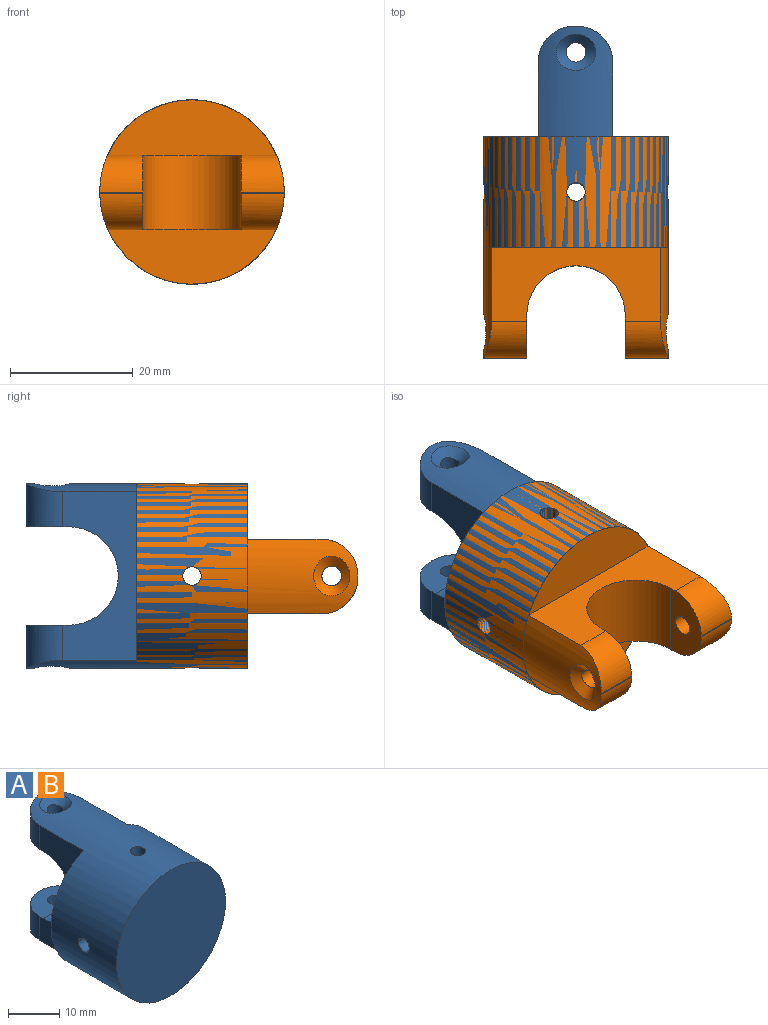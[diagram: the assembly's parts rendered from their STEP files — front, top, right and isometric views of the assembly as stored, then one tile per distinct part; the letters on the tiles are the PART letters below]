
ASSEMBLY  parts=2 mates=1
PART A: 23 faces, bbox 30x36x30 mm
  f0: cylinder r=1.5mm len=14.93mm, axis (1,0,0), area 132.6mm2, adj f2,f21,f22
  f1: plane 7x0.16mm, normal (0,1,0), area 1.1mm2, adj f2,f6,f14,f15
  f2: cylinder r=15mm len=36mm, axis (0,1,0), area 2026.3mm2, adj f0,f1,f3,f7,f10,f11,f12,f13
  f3: plane 7x0.16mm, normal (0,1,0), area 1.1mm2, adj f2,f5,f16,f17
  f4: cylinder r=8mm len=16mm, axis (1,0,0), area 305.7mm2, adj f5,f6,f11,f13
  f5: plane 12.16x7mm, normal (0,0,1), area 61.7mm2, adj f3,f4,f9,f11,f13,f16,f17
  f6: plane 12.16x7mm, normal (0,0,-1), area 61.7mm2, adj f1,f4,f8,f11,f13,f14,f15
  f7: plane 30x30mm, normal (0,-1,0), area 706.9mm2, adj f2
  f8: cylinder r=1.6mm len=5.65mm, axis (0,0,1), area 56.8mm2, adj f6,f18
  f9: cylinder r=1.6mm len=5.33mm, axis (0,0,1), area 53.6mm2, adj f5,f19
  f10: plane 27.5x9mm, normal (0,1,0), area 178.4mm2, adj f2,f11
  f11: plane 27.5x12mm, normal (1,0,0), area 213.4mm2, adj f2,f4,f5,f6,f10,f15,f16
  f12: plane 27.35x8.84mm, normal (0,1,0), area 173.9mm2, adj f2,f13
  f13: plane 27.35x12mm, normal (-1,0,0), area 211.7mm2, adj f2,f4,f5,f6,f12,f14,f17
  f14: cylinder r=6mm len=7mm, axis (0,0,-1), area 59.7mm2, adj f1,f2,f6,f13
  f15: cylinder r=6mm len=7mm, axis (0,0,1), area 60.1mm2, adj f1,f2,f6,f11
  f16: cylinder r=6mm len=7mm, axis (0,0,1), area 60.1mm2, adj f2,f3,f5,f11
  f17: cylinder r=6mm len=7mm, axis (0,0,-1), area 59.7mm2, adj f2,f3,f5,f13
  f18: bspline ~6.48x5.9mm, area 29.7mm2, adj f2,f8
  f19: bspline ~6.47x5.89mm, area 29.7mm2, adj f2,f9
  f20: cylinder r=1.5mm len=14.93mm, axis (1,0,0), area 132.6mm2, adj f2,f21,f22
  f21: cylinder r=1.5mm len=15mm, axis (0,0,1), area 141.4mm2, adj f0,f2,f20
  f22: cylinder r=1.5mm len=14.93mm, axis (0,0,1), area 133.6mm2, adj f0,f2,f20
PART B: same geometry as A
PLACE A t=(-3.18,5.14,-3.04)mm
PLACE B rot(axis=(0.71,0,0.71),180deg) t=(-3.18,-48.86,-3.04)mm
MATE planar B.f2 <-> A.f2  axis (0,1,0) through (-3.18,-12.86,-3.04)mm
